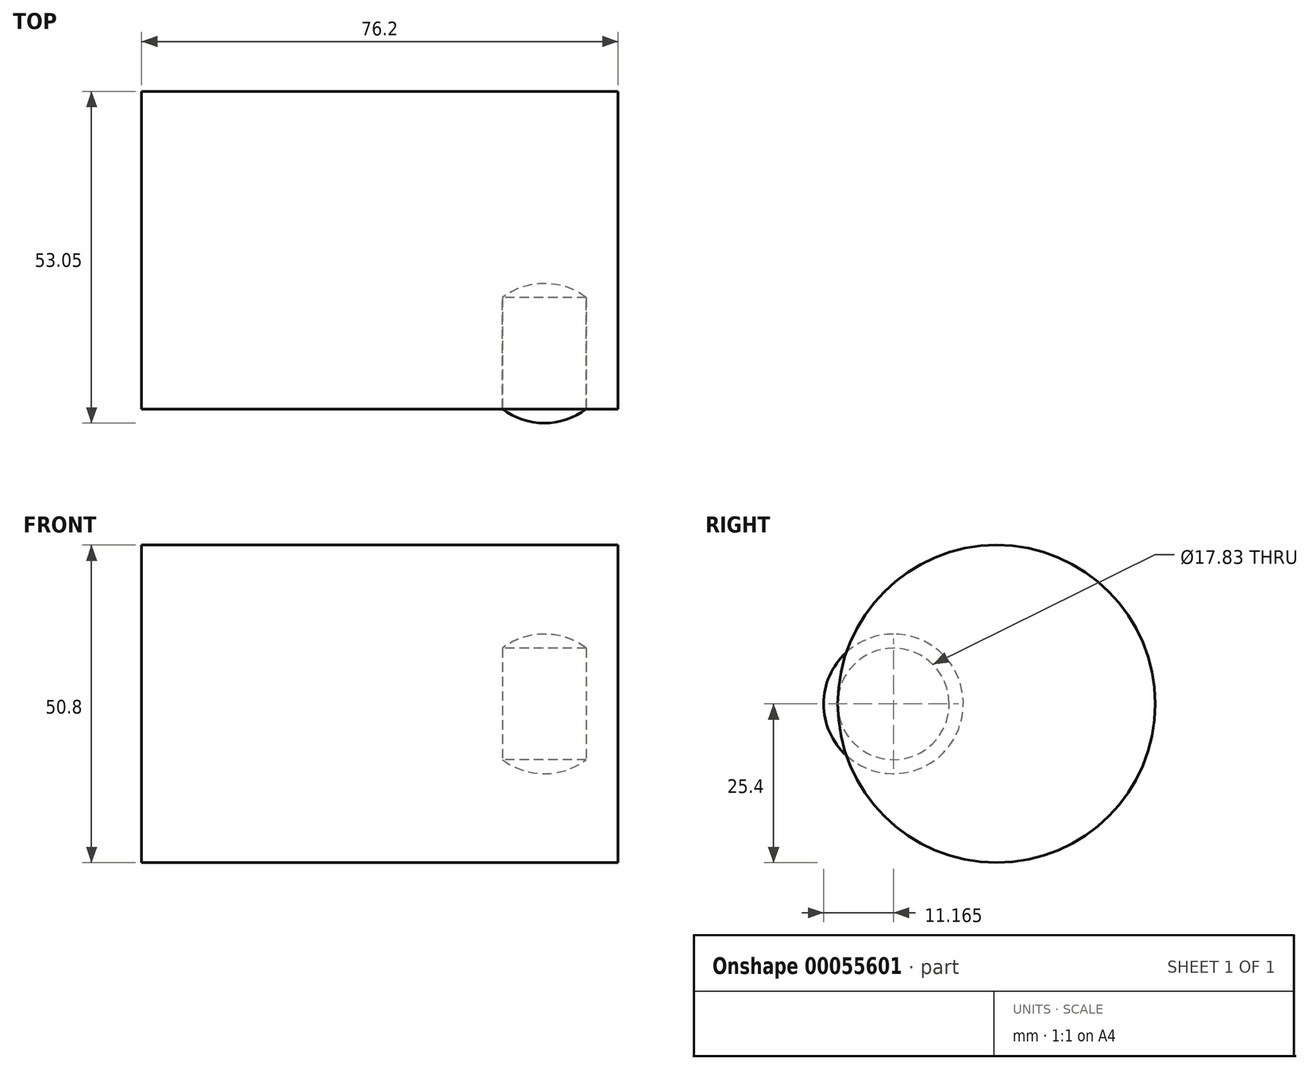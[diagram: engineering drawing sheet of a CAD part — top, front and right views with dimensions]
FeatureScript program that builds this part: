
annotation { "Feature Type Name" : "Feature", "Feature Type Description" : "" }
export const myFeature = defineFeature(function(context is Context, id is Id, definition is map)
    precondition{}
    {
        {
            var Q0;
            Q0=qCreatedBy(makeId("Right.planeOp"),FACE);
            var sketch = newSketch(context, id + "F0", { "sketchPlane" : qUnion([Q0])});
            skCircle(sketch, "E0", {"center": v(0, 0) * mm, "radius": 25.4 * mm});
            skSolve(sketch);
        }
        {
            var Q0;
            Q0 = qSketchRegion(id + "F0", true);
            extrude(context, id + "F1", {"entities" : qUnion([Q0]), "depth" : 76.2 * mm});
        }
        {
            var Q0;
            Q0=qCreatedBy(makeId("Top.planeOp"),FACE);
            var sketch = newSketch(context, id + "F2", { "sketchPlane" : qUnion([Q0])});
            skLineSegment(sketch, "E1", {"start": v(76.2, -25.4) * mm, "end": v(0, -25.4) * mm});
            skLineSegment(sketch, "E2", {"start": v(0, 25.4) * mm, "end": v(76.2, 25.4) * mm});
            skCircle(sketch, "E3", {"center": v(64.4, -16.49) * mm, "radius": 11.17 * mm});
            skLineSegment(sketch, "E4", {"start": v(53.24, -16.49) * mm, "end": v(75.57, -16.49) * mm});
            skSolve(sketch);
        }
        {
            var Q0;
            {var subQ0=sQuery(id+"F2.wireOp",EDGE,"E3");var subQ1=sQuery(id+"F2.wireOp",EDGE,"E1");var subQ2=makeQuery(id+"F2.imprint","INTERSECT",VERTEX,{"disambiguationData":[OD(0.0)],"derivedFrom":[subQ1,subQ0]});Q0=makeQuery(id+"F2.imprint","IMPRINT",FACE,{"disambiguationData":[TD([[makeQuery(id+"F2.imprint","IMPRINT",EDGE,{"disambiguationData":[TD([[subQ2,1.0]])],"derivedFrom":subQ1}),1.0]])]});}
            var Q1;
            Q1=sQuery(id+"F2.wireOp",EDGE,"E4");
            revolve(context, id + "F3", {"entities" : qUnion([Q0]), "axis" : qUnion([Q1]), "revolveType" : RevolveType.FULL});
        }
    });
